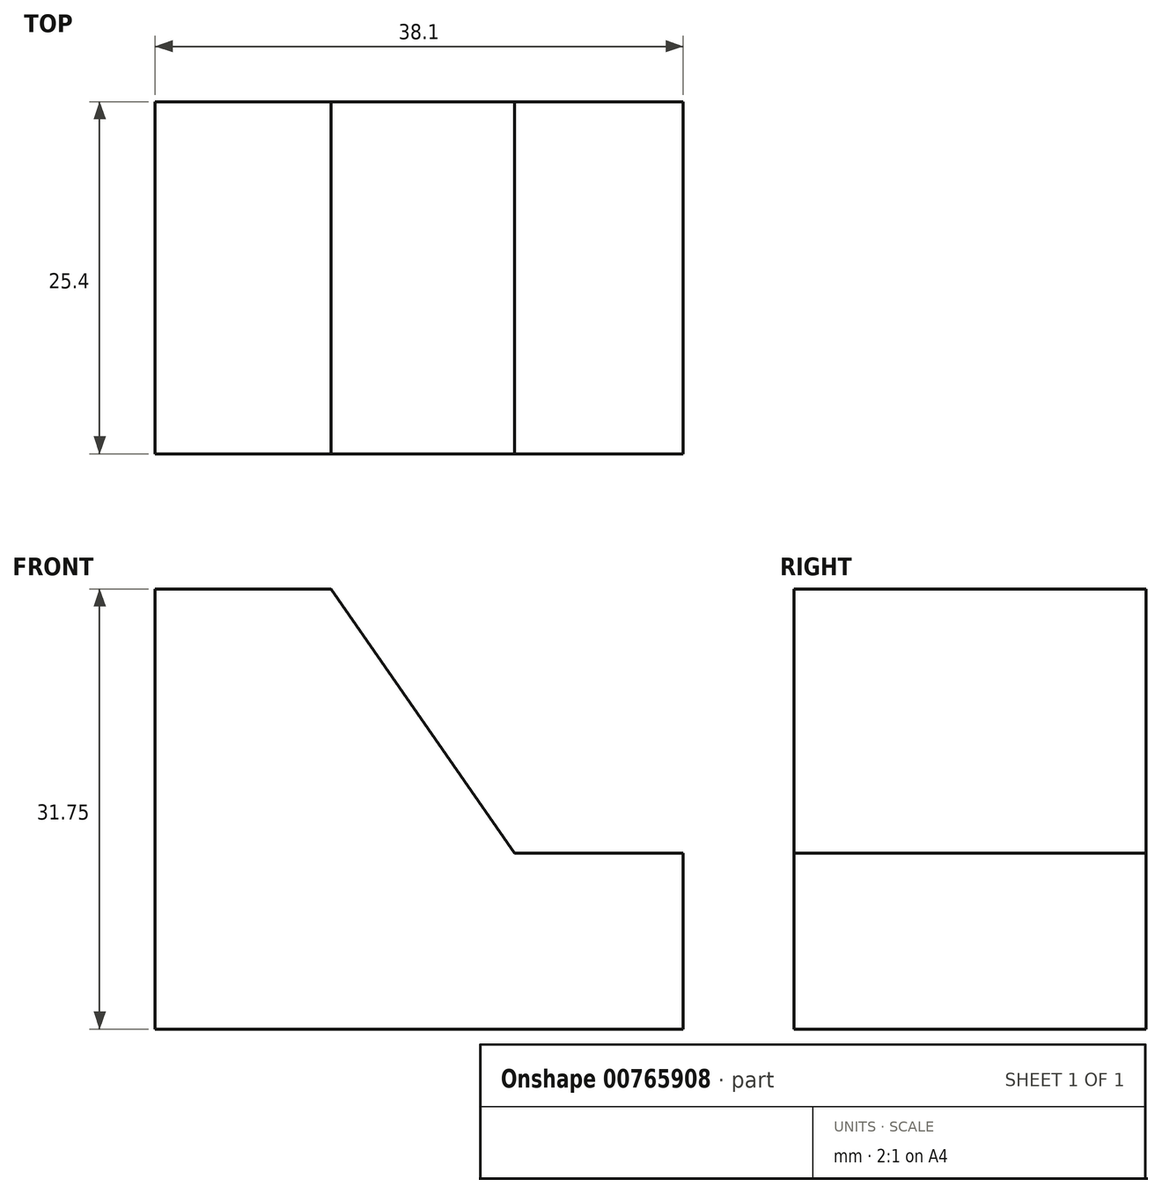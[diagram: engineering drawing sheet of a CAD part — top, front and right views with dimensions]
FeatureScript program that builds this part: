
annotation { "Feature Type Name" : "Feature", "Feature Type Description" : "" }
export const myFeature = defineFeature(function(context is Context, id is Id, definition is map)
    precondition{}
    {
        {
            var Q0;
            Q0=qCreatedBy(makeId("Front.planeOp"),FACE);
            var sketch = newSketch(context, id + "F0", { "sketchPlane" : qUnion([Q0])});
            skLineSegment(sketch, "E0", {"start": v(0, 0) * mm, "end": v(38.1, 0) * mm});
            skLineSegment(sketch, "E1", {"start": v(38.1, 0) * mm, "end": v(38.1, 12.7) * mm});
            skLineSegment(sketch, "E2", {"start": v(38.1, 12.7) * mm, "end": v(25.93, 12.7) * mm});
            skLineSegment(sketch, "E3", {"start": v(0, 0) * mm, "end": v(0, 31.75) * mm});
            skLineSegment(sketch, "E4", {"start": v(0, 31.75) * mm, "end": v(12.7, 31.75) * mm});
            skLineSegment(sketch, "E5", {"start": v(25.93, 12.7) * mm, "end": v(12.7, 31.75) * mm});
            skSolve(sketch);
        }
        {
            var Q0;
            Q0 = qSketchRegion(id + "F0", true);
            extrude(context, id + "F1", {"entities" : qUnion([Q0]), "depth" : 25.4 * mm, "offsetDistance" : 25.4 * mm});
        }
    });
